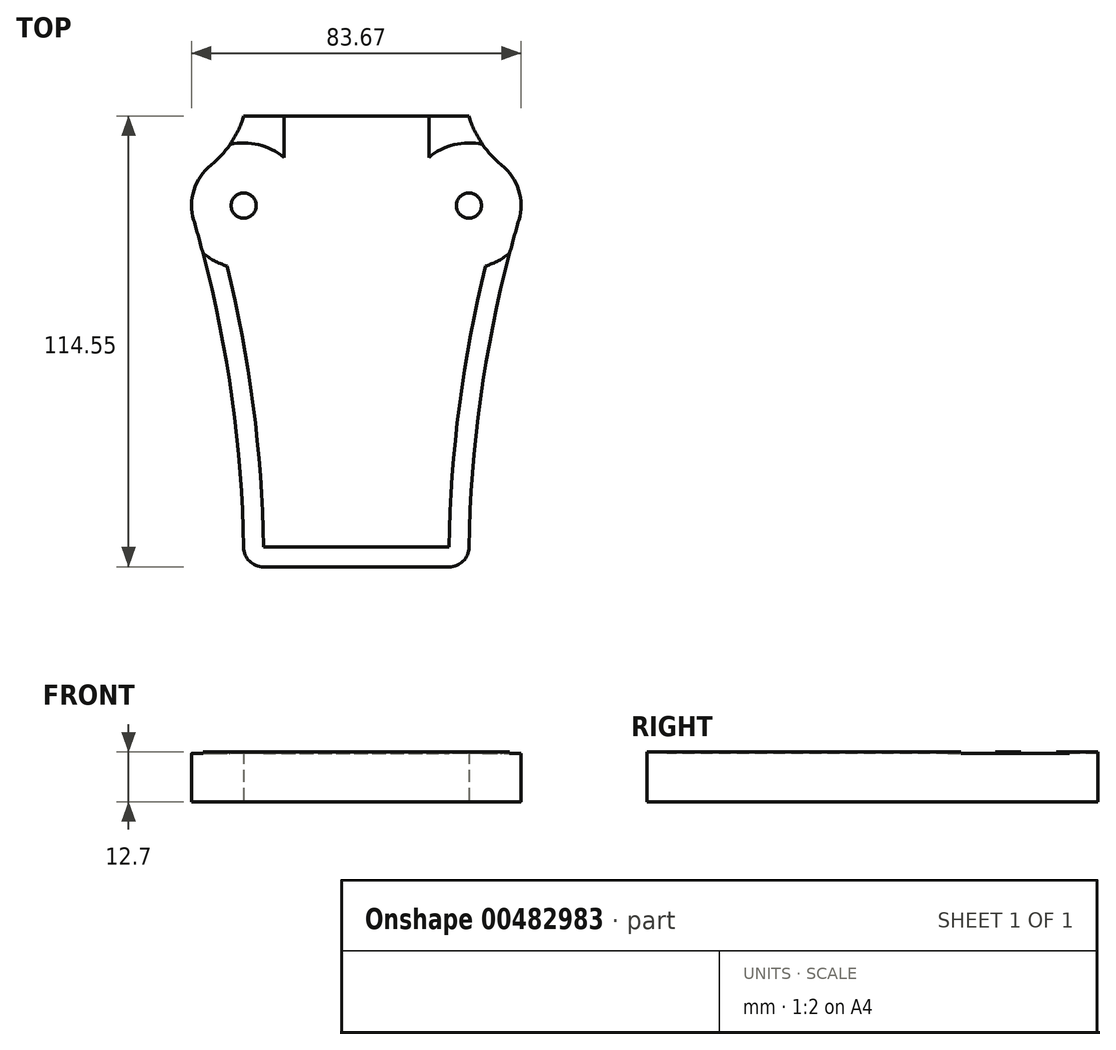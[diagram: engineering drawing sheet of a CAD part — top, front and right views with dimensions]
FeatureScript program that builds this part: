
annotation { "Feature Type Name" : "Feature", "Feature Type Description" : "" }
export const myFeature = defineFeature(function(context is Context, id is Id, definition is map)
    precondition{}
    {
        {
            var Q0;
            Q0=qCreatedBy(makeId("Top.planeOp"),FACE);
            var sketch = newSketch(context, id + "F0", { "sketchPlane" : qUnion([Q0])});
            skLineSegment(sketch, "E0.bottom", {"start": v(0, 0) * mm, "end": v(57.2, 0) * mm});
            skLineSegment(sketch, "E0.top", {"start": v(0, 105.03) * mm, "end": v(57.2, 105.03) * mm});
            skLineSegment(sketch, "E0.left", {"start": v(0, 0) * mm, "end": v(0, 105.03) * mm});
            skLineSegment(sketch, "E0.right", {"start": v(57.2, 0) * mm, "end": v(57.2, 105.03) * mm});
            skArc(sketch, "E1", {"start": v(0, 105.03) * mm, "mid": v(-13.23, 91.8) * mm, "end": v(0, 78.57) * mm});
            skArc(sketch, "E2", {"start": v(57.2, 78.57) * mm, "mid": v(70.44, 91.8) * mm, "end": v(57.2, 105.03) * mm});
            skCircle(sketch, "E3", {"center": v(0, 91.8) * mm, "radius": 13.23 * mm, "construction": true});
            skCircle(sketch, "E4", {"center": v(57.2, 91.8) * mm, "radius": 13.23 * mm, "construction": true});
            skLineSegment(sketch, "E5", {"start": v(13.23, 91.8) * mm, "end": v(28.58, 91.8) * mm, "construction": true});
            skLineSegment(sketch, "E6", {"start": v(28.58, 91.8) * mm, "end": v(28.63, 91.8) * mm, "construction": true});
            skLineSegment(sketch, "E7", {"start": v(28.63, 91.8) * mm, "end": v(43.98, 91.8) * mm, "construction": true});
            skArc(sketch, "E8", {"start": v(0, 0) * mm, "mid": v(-3.19, 44.49) * mm, "end": v(-12.7, 88.06) * mm});
            skArc(sketch, "E9", {"start": v(69.9, 88.06) * mm, "mid": v(60.4, 44.49) * mm, "end": v(57.2, 0) * mm});
            skArc(sketch, "E10", {"start": v(0, 0) * mm, "mid": v(-3.19, 44.49) * mm, "end": v(-12.7, 88.06) * mm, "construction": true});
            skLineSegment(sketch, "E11", {"start": v(-1.18, 111.38) * mm, "end": v(58.39, 111.38) * mm});
            skArc(sketch, "E12", {"start": v(-8.34, 102.07) * mm, "mid": v(-4.21, 106.3) * mm, "end": v(-1.18, 111.38) * mm});
            skArc(sketch, "E13", {"start": v(58.39, 111.38) * mm, "mid": v(61.42, 106.3) * mm, "end": v(65.55, 102.07) * mm});
            skLineSegment(sketch, "E14", {"start": v(0, 114.55) * mm, "end": v(57.2, 114.55) * mm});
            skArc(sketch, "E15", {"start": v(-1.18, 111.38) * mm, "mid": v(-0.54, 112.95) * mm, "end": v(0, 114.55) * mm});
            skArc(sketch, "E16", {"start": v(57.2, 114.55) * mm, "mid": v(57.75, 112.95) * mm, "end": v(58.39, 111.38) * mm});
            skSolve(sketch);
        }
        {
            var Q0;
            Q0=qSketchRegion(id+"F0",true);
            extrude(context, id + "F1", {"entities" : qUnion([Q0]), "depth" : 12.7 * mm});
        }
        {
            var Q0;
            Q0=makeQuery(id+"F1.opExtrude","SWEPT_EDGE",EDGE,{"disambiguationData":[OSD([sQuery(id+"F0.wireOp",EDGE,"E0.bottom"),sQuery(id+"F0.wireOp",EDGE,"E0.left"),sQuery(id+"F0.wireOp",EDGE,"E8")])]});
            var Q1;
            Q1=makeQuery(id+"F1.opExtrude","SWEPT_EDGE",EDGE,{"disambiguationData":[OSD([sQuery(id+"F0.wireOp",EDGE,"E0.bottom"),sQuery(id+"F0.wireOp",EDGE,"E0.right"),sQuery(id+"F0.wireOp",EDGE,"E9")])]});
            fillet(context, id + "F2", {"entities" : qUnion([Q0, Q1]), "radius" : 5.08 * mm, "tangentPropagation" : true, "allowEdgeOverflow" : false});
        }
        {
            var Q0;
            Q0=makeQuery(id+"F1.opExtrude","CAP_FACE",FACE,{"disambiguationData":[OSD([sQuery(id+"F0.wireOp",EDGE,"E0.bottom"),sQuery(id+"F0.wireOp",EDGE,"E1"),sQuery(id+"F0.wireOp",EDGE,"E2"),sQuery(id+"F0.wireOp",EDGE,"E8"),sQuery(id+"F0.wireOp",EDGE,"E9"),sQuery(id+"F0.wireOp",EDGE,"E12"),sQuery(id+"F0.wireOp",EDGE,"E13"),sQuery(id+"F0.wireOp",EDGE,"E14"),sQuery(id+"F0.wireOp",EDGE,"E15"),sQuery(id+"F0.wireOp",EDGE,"E16")])],"isStart":false});
            var sketch = newSketch(context, id + "F3", { "sketchPlane" : qUnion([Q0])});
            skArc(sketch, "E17", {"start": v(5.04, 5.08) * mm, "mid": v(1.47, 47.72) * mm, "end": v(-7.82, 89.5) * mm});
            skArc(sketch, "E18", {"start": v(-5.14, 98.13) * mm, "mid": v(-7.78, 94.22) * mm, "end": v(-7.82, 89.5) * mm});
            skLineSegment(sketch, "E19", {"start": v(5.04, 5.08) * mm, "end": v(28.6, 5.08) * mm});
            skLineSegment(sketch, "E20", {"start": v(1.9, 106.3) * mm, "end": v(6.54, 106.3) * mm});
            skArc(sketch, "E21", {"start": v(-5.14, 98.13) * mm, "mid": v(-1.25, 101.9) * mm, "end": v(1.9, 106.3) * mm});
            skLineSegment(sketch, "E22", {"start": v(28.6, 5.08) * mm, "end": v(28.6, 106.3) * mm, "construction": true});
            skLineSegment(sketch, "E23.MirrorCS", {"start": v(55.3, 106.3) * mm, "end": v(50.67, 106.3) * mm});
            skArc(sketch, "E24.MirrorCS", {"start": v(62.35, 98.13) * mm, "mid": v(58.46, 101.9) * mm, "end": v(55.3, 106.3) * mm});
            skArc(sketch, "E25.MirrorCS", {"start": v(62.35, 98.13) * mm, "mid": v(65, 94.22) * mm, "end": v(65.03, 89.5) * mm});
            skArc(sketch, "E26.MirrorCS", {"start": v(52.17, 5.08) * mm, "mid": v(55.74, 47.72) * mm, "end": v(65.03, 89.5) * mm});
            skLineSegment(sketch, "E27.MirrorCS", {"start": v(52.17, 5.08) * mm, "end": v(28.6, 5.08) * mm});
            skLineSegment(sketch, "E28.bottom", {"start": v(10.19, 114.55) * mm, "end": v(47.02, 114.55) * mm});
            skLineSegment(sketch, "E28.top", {"start": v(15.68, 89.15) * mm, "end": v(47.02, 89.15) * mm});
            skLineSegment(sketch, "E28.left", {"start": v(10.19, 114.55) * mm, "end": v(10.19, 104.01) * mm});
            skLineSegment(sketch, "E28.right", {"start": v(47.02, 114.55) * mm, "end": v(47.02, 89.15) * mm});
            skArc(sketch, "E29", {"start": v(10.19, 104.01) * mm, "mid": v(-14.92, 86.28) * mm, "end": v(15.68, 89.15) * mm});
            skLineSegment(sketch, "E30.trimOffspring", {"start": v(10.19, 106.3) * mm, "end": v(28.6, 106.3) * mm});
            skPoint(sketch, "E31.orphan", {"position": v(10.19, 89.15) * mm});
            skArc(sketch, "E32.MirrorCS", {"start": v(47.02, 104.01) * mm, "mid": v(72.13, 86.28) * mm, "end": v(41.53, 89.15) * mm});
            skLineSegment(sketch, "E33.trimOffspring", {"start": v(47.02, 106.3) * mm, "end": v(28.6, 106.3) * mm});
            skCircle(sketch, "E34", {"center": v(0, 91.8) * mm, "radius": 3.2 * mm});
            skCircle(sketch, "E35", {"center": v(57.2, 91.8) * mm, "radius": 3.2 * mm});
            skSolve(sketch);
        }
        {
            var Q0;
            Q0=qSketchRegion(id+"F3",true);
            extrude(context, id + "F4", {"entities" : qUnion([Q0]), "operationType" : NewBodyOperationType.REMOVE, "oppositeDirection" : true, "depth" : (.5 - (1 / 8)) * mm, "offsetDistance" : 25.4 * mm});
        }
    });
